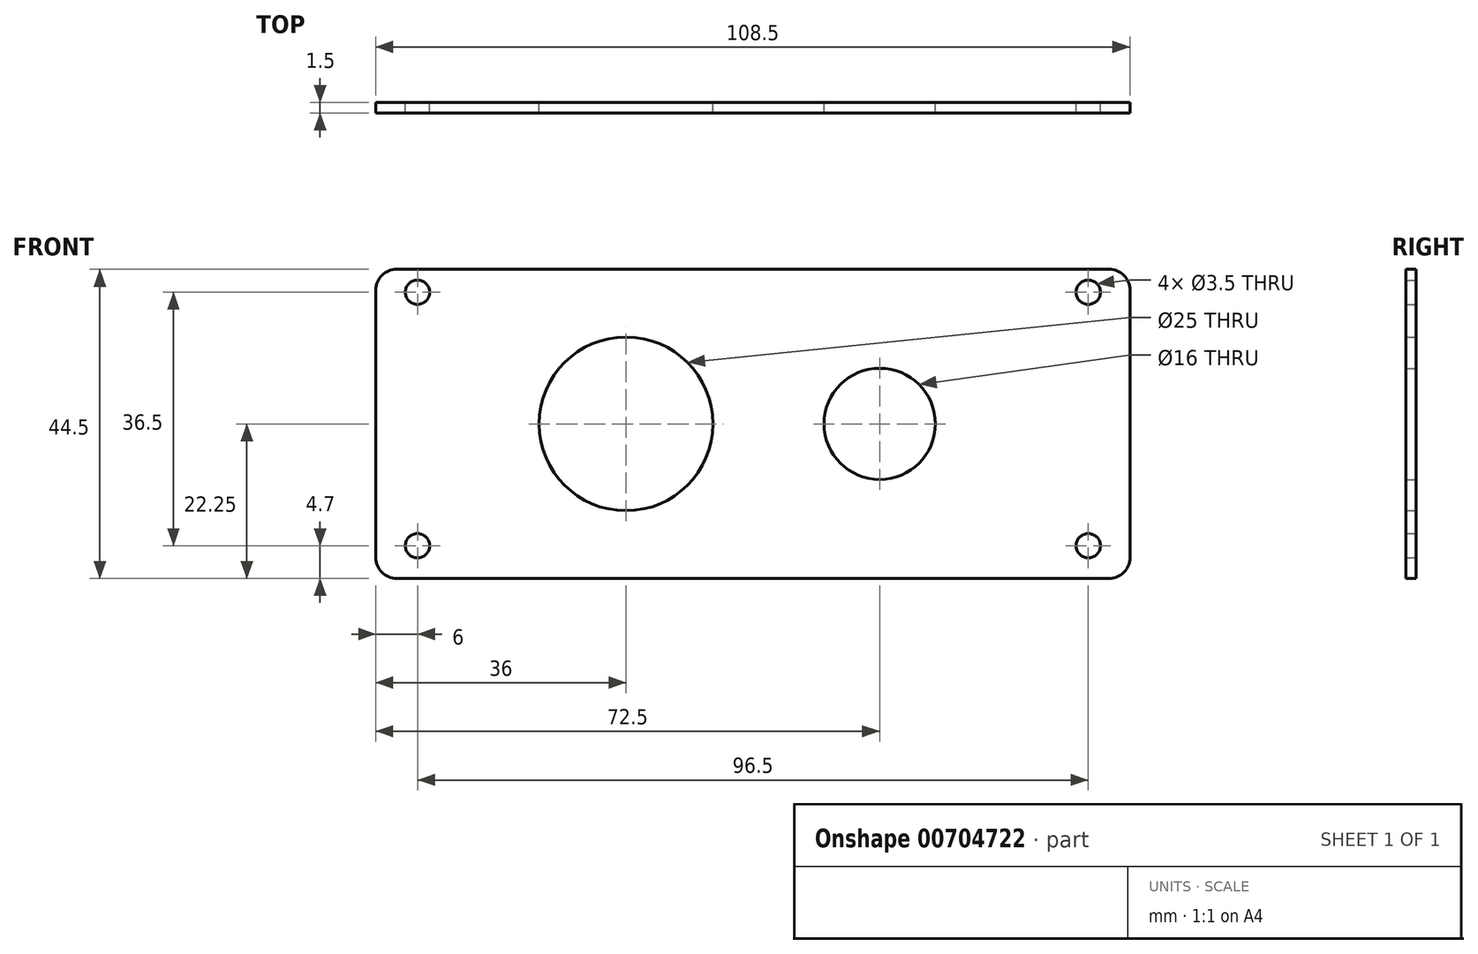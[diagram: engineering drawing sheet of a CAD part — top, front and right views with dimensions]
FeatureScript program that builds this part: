
annotation { "Feature Type Name" : "Feature", "Feature Type Description" : "" }
export const myFeature = defineFeature(function(context is Context, id is Id, definition is map)
    precondition{}
    {
        {
            var Q0;
            Q0=qCreatedBy(makeId("Front.planeOp"),FACE);
            var sketch = newSketch(context, id + "F0", { "sketchPlane" : qUnion([Q0])});
            skLineSegment(sketch, "E0.bottom", {"start": v(54.25, -22.25) * mm, "end": v(-54.25, -22.25) * mm});
            skLineSegment(sketch, "E0.top", {"start": v(54.25, 22.25) * mm, "end": v(-54.25, 22.25) * mm});
            skLineSegment(sketch, "E0.left", {"start": v(54.25, -22.25) * mm, "end": v(54.25, 22.25) * mm});
            skLineSegment(sketch, "E0.right", {"start": v(-54.25, -22.25) * mm, "end": v(-54.25, 22.25) * mm});
            skPoint(sketch, "E0.middle", {"position": v(0, 0) * mm});
            skCircle(sketch, "E1", {"center": v(-18.25, 0) * mm, "radius": 12.5 * mm});
            skCircle(sketch, "E2", {"center": v(18.25, 0) * mm, "radius": 8 * mm});
            skCircle(sketch, "E3", {"center": v(-48.25, -17.55) * mm, "radius": 1.75 * mm});
            skCircle(sketch, "E4", {"center": v(48.25, -17.55) * mm, "radius": 1.75 * mm});
            skCircle(sketch, "E5", {"center": v(48.25, 18.95) * mm, "radius": 1.75 * mm});
            skCircle(sketch, "E6", {"center": v(-48.25, 18.95) * mm, "radius": 1.75 * mm});
            skSolve(sketch);
        }
        {
            var Q0;
            Q0=makeQuery(id+"F0.imprint","IMPRINT",FACE,{"disambiguationData":[TD([[makeQuery(id+"F0.imprint","IMPRINT",EDGE,{"derivedFrom":sQuery(id+"F0.wireOp",EDGE,"E0.bottom")}),-1.0]])]});
            extrude(context, id + "F1", {"entities" : qUnion([Q0]), "depth" : 1.5 * mm, "offsetDistance" : 25 * mm});
        }
        {
            var Q0;
            Q0=makeQuery(id+"F1.opExtrude","SWEPT_EDGE",EDGE,{"disambiguationData":[OSD([sQuery(id+"F0.wireOp",EDGE,"E0.top"),sQuery(id+"F0.wireOp",EDGE,"E0.left")])]});
            var Q1;
            Q1=makeQuery(id+"F1.opExtrude","SWEPT_EDGE",EDGE,{"disambiguationData":[OSD([sQuery(id+"F0.wireOp",EDGE,"E0.bottom"),sQuery(id+"F0.wireOp",EDGE,"E0.left")])]});
            var Q2;
            Q2=makeQuery(id+"F1.opExtrude","SWEPT_EDGE",EDGE,{"disambiguationData":[OSD([sQuery(id+"F0.wireOp",EDGE,"E0.bottom"),sQuery(id+"F0.wireOp",EDGE,"E0.right")])]});
            var Q3;
            Q3=makeQuery(id+"F1.opExtrude","SWEPT_EDGE",EDGE,{"disambiguationData":[OSD([sQuery(id+"F0.wireOp",EDGE,"E0.top"),sQuery(id+"F0.wireOp",EDGE,"E0.right")])]});
            fillet(context, id + "F2", {"entities" : qUnion([Q0, Q1, Q2, Q3]), "tangentPropagation" : true, "radius" : 3 * mm, "defaultsChanged" : false, "vertexSettings" : [], "allowEdgeOverflow" : false});
        }
    });
